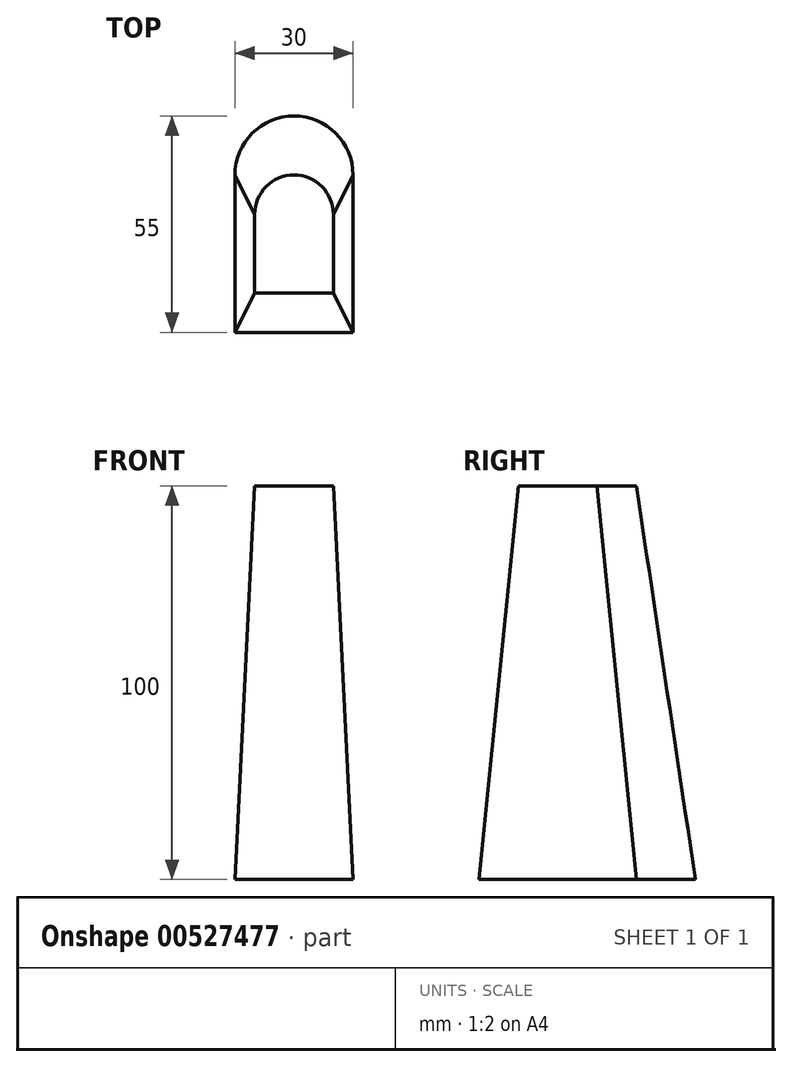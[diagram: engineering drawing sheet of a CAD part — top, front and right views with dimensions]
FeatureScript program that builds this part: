
annotation { "Feature Type Name" : "Feature", "Feature Type Description" : "" }
export const myFeature = defineFeature(function(context is Context, id is Id, definition is map)
    precondition{}
    {
        {
            var Q0;
            Q0=qCreatedBy(makeId("Top.planeOp"),FACE);
            var sketch = newSketch(context, id + "F0", { "sketchPlane" : qUnion([Q0])});
            skLineSegment(sketch, "E0.top", {"start": v(-15, -20) * mm, "end": v(15, -20) * mm});
            skLineSegment(sketch, "E0.left", {"start": v(-15, 20) * mm, "end": v(-15, -20) * mm});
            skLineSegment(sketch, "E0.right", {"start": v(15, 20) * mm, "end": v(15, -20) * mm});
            skPoint(sketch, "E0.middle", {"position": v(0, 0) * mm});
            skArc(sketch, "E1", {"start": v(15, 20) * mm, "mid": v(0, 35) * mm, "end": v(-15, 20) * mm});
            skSolve(sketch);
        }
        {
            var Q0;
            Q0=qCreatedBy(makeId("Top.planeOp"),FACE);
            cPlane(context, id + "F1", {"entities" : qUnion([Q0]), "cplaneType" : CPlaneType.OFFSET, "offset" : 100 * mm, "width" : 150 * mm, "height" : 150 * mm});
        }
        {
            var Q0;
            Q0=qCreatedBy(id+"F1.planeOp",FACE);
            var sketch = newSketch(context, id + "F2", { "sketchPlane" : qUnion([Q0])});
            skPoint(sketch, "E2.0", {"position": v(0, 0) * mm});
            skLineSegment(sketch, "E3.top", {"start": v(10, -10) * mm, "end": v(-10, -10) * mm});
            skLineSegment(sketch, "E3.left", {"start": v(10, 10) * mm, "end": v(10, -10) * mm});
            skLineSegment(sketch, "E3.right", {"start": v(-10, 10) * mm, "end": v(-10, -10) * mm});
            skArc(sketch, "E4", {"start": v(-10, 10) * mm, "mid": v(0, 20) * mm, "end": v(10, 10) * mm});
            skSolve(sketch);
        }
        {
            var Q0;
            Q0=makeQuery(id+"F0.imprint","IMPRINT",FACE,{"disambiguationData":[TD([[makeQuery(id+"F0.imprint","IMPRINT",EDGE,{"derivedFrom":sQuery(id+"F0.wireOp",EDGE,"E0.top")}),1.0]])]});
            var Q1;
            Q1=makeQuery(id+"F2.imprint","IMPRINT",FACE,{"disambiguationData":[TD([[makeQuery(id+"F2.imprint","IMPRINT",EDGE,{"derivedFrom":sQuery(id+"F2.wireOp",EDGE,"E3.top")}),-1.0]])]});
            loft(context, id + "F3", {"sheetProfilesArray" : [{ "sheetProfileEntities" : qUnion([Q0]) }, { "sheetProfileEntities" : qUnion([Q1]) }]});
        }
    });
